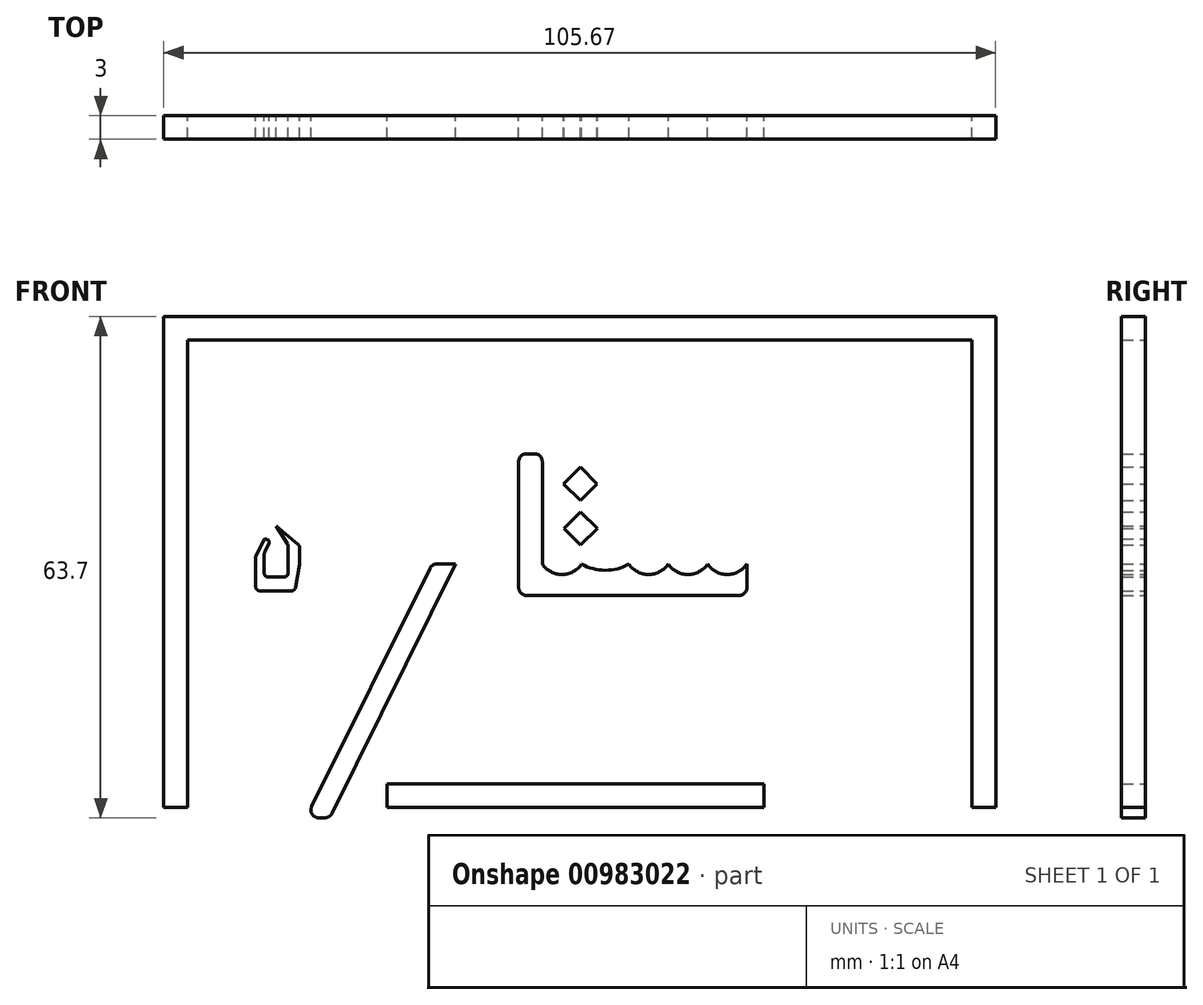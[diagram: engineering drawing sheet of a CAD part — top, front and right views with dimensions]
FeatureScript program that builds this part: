
annotation { "Feature Type Name" : "Feature", "Feature Type Description" : "" }
export const myFeature = defineFeature(function(context is Context, id is Id, definition is map)
    precondition{}
    {
        {
            var Q0;
            Q0=qCreatedBy(makeId("Front.planeOp"),FACE);
            var sketch = newSketch(context, id + "F0", { "sketchPlane" : qUnion([Q0])});
            skArc(sketch, "E0", {"start": v(-5, 0) * mm, "mid": v(-2.5, -1.34) * mm, "end": v(0, 0) * mm});
            skArc(sketch, "E1", {"start": v(-10, 0) * mm, "mid": v(-7.5, -1.34) * mm, "end": v(-5, 0) * mm});
            skArc(sketch, "E2", {"start": v(-15, 0) * mm, "mid": v(-12.5, -1.34) * mm, "end": v(-10, 0) * mm});
            skArc(sketch, "E3", {"start": v(-21, 0) * mm, "mid": v(-18, -0.8) * mm, "end": v(-15, 0) * mm});
            skArc(sketch, "E4", {"start": v(-26, 0) * mm, "mid": v(-23.5, -1.34) * mm, "end": v(-21, 0) * mm});
            skLineSegment(sketch, "E5", {"start": v(-26, 0) * mm, "end": v(-26, 13) * mm});
            skLineSegment(sketch, "E6", {"start": v(-29, 13) * mm, "end": v(-29, -3) * mm});
            skLineSegment(sketch, "E7", {"start": v(-28, -4) * mm, "end": v(-1, -4) * mm});
            skLineSegment(sketch, "E8", {"start": v(-27, 14) * mm, "end": v(-28, 14) * mm});
            skLineSegment(sketch, "E9", {"start": v(0, -3) * mm, "end": v(0, 0) * mm});
            skPoint(sketch, "E10.visualSharp", {"position": v(-29, 14) * mm});
            skArc(sketch, "E10.filletArc", {"start": v(-28, 14) * mm, "mid": v(-28.7, 13.7) * mm, "end": v(-29, 13) * mm});
            skPoint(sketch, "E11.visualSharp", {"position": v(-26, 14) * mm});
            skArc(sketch, "E11.filletArc", {"start": v(-26, 13) * mm, "mid": v(-26.3, 13.7) * mm, "end": v(-27, 14) * mm});
            skPoint(sketch, "E12.visualSharp", {"position": v(-29, -4) * mm});
            skArc(sketch, "E12.filletArc", {"start": v(-29, -3) * mm, "mid": v(-28.7, -3.7) * mm, "end": v(-28, -4) * mm});
            skPoint(sketch, "E13.visualSharp", {"position": v(0, -4) * mm});
            skArc(sketch, "E13.filletArc", {"start": v(-1, -4) * mm, "mid": v(-0.3, -3.7) * mm, "end": v(0, -3) * mm});
            skLineSegment(sketch, "E14", {"start": v(-39.38, 0) * mm, "end": v(-37, 0) * mm});
            skLineSegment(sketch, "E15", {"start": v(-37, 0) * mm, "end": v(-52.72, -31.7) * mm});
            skLineSegment(sketch, "E16", {"start": v(-53.62, -32.25) * mm, "end": v(-54.39, -32.25) * mm});
            skLineSegment(sketch, "E17", {"start": v(-55.28, -30.8) * mm, "end": v(-40.28, -0.56) * mm});
            skPoint(sketch, "E18.visualSharp", {"position": v(-40, 0) * mm});
            skArc(sketch, "E18.filletArc", {"start": v(-39.38, 0) * mm, "mid": v(-39.9, -0.15) * mm, "end": v(-40.28, -0.56) * mm});
            skPoint(sketch, "E19.visualSharp", {"position": v(-56, -32.25) * mm});
            skArc(sketch, "E19.filletArc", {"start": v(-55.28, -30.8) * mm, "mid": v(-55.24, -31.78) * mm, "end": v(-54.39, -32.25) * mm});
            skPoint(sketch, "E20.visualSharp", {"position": v(-53, -32.25) * mm});
            skArc(sketch, "E20.filletArc", {"start": v(-53.62, -32.25) * mm, "mid": v(-53.1, -32.1) * mm, "end": v(-52.72, -31.7) * mm});
            skLineSegment(sketch, "E21.bottom", {"start": v(-21.12, 6.63) * mm, "end": v(-19, 4.51) * mm});
            skLineSegment(sketch, "E21.top", {"start": v(-23.24, 4.51) * mm, "end": v(-21.12, 2.39) * mm});
            skLineSegment(sketch, "E21.left", {"start": v(-21.12, 6.63) * mm, "end": v(-23.24, 4.51) * mm});
            skLineSegment(sketch, "E21.right", {"start": v(-19, 4.51) * mm, "end": v(-21.12, 2.39) * mm});
            skLineSegment(sketch, "E22.bottom", {"start": v(-21.17, 12.3) * mm, "end": v(-19.05, 10.17) * mm});
            skLineSegment(sketch, "E22.top", {"start": v(-23.3, 10.17) * mm, "end": v(-21.17, 8.05) * mm});
            skLineSegment(sketch, "E22.left", {"start": v(-21.17, 12.3) * mm, "end": v(-23.3, 10.17) * mm});
            skLineSegment(sketch, "E22.right", {"start": v(-19.05, 10.17) * mm, "end": v(-21.17, 8.05) * mm});
            skLineSegment(sketch, "E23.bottom", {"start": v(-71.08, 31.45) * mm, "end": v(-74.08, 31.45) * mm});
            skLineSegment(sketch, "E23.top", {"start": v(-71.08, -30.93) * mm, "end": v(-74.08, -30.93) * mm});
            skLineSegment(sketch, "E23.left", {"start": v(-71.08, 31.45) * mm, "end": v(-71.08, -30.93) * mm});
            skLineSegment(sketch, "E23.right", {"start": v(-74.08, 31.45) * mm, "end": v(-74.08, -30.93) * mm});
            skLineSegment(sketch, "E24.bottom", {"start": v(-71.08, 31.45) * mm, "end": v(28.6, 31.45) * mm});
            skLineSegment(sketch, "E24.top", {"start": v(-71.08, 28.45) * mm, "end": v(28.6, 28.45) * mm});
            skLineSegment(sketch, "E24.left", {"start": v(-71.08, 31.45) * mm, "end": v(-71.08, 28.45) * mm});
            skLineSegment(sketch, "E24.right", {"start": v(28.6, 31.45) * mm, "end": v(28.6, 28.45) * mm});
            skLineSegment(sketch, "E25.bottom", {"start": v(28.6, 31.45) * mm, "end": v(31.6, 31.45) * mm});
            skLineSegment(sketch, "E25.top", {"start": v(28.6, -30.93) * mm, "end": v(31.6, -30.93) * mm});
            skLineSegment(sketch, "E25.left", {"start": v(28.6, 31.45) * mm, "end": v(28.6, -30.93) * mm});
            skLineSegment(sketch, "E25.right", {"start": v(31.6, 31.45) * mm, "end": v(31.6, -30.93) * mm});
            skLineSegment(sketch, "E26.bottom", {"start": v(-45.73, -27.93) * mm, "end": v(2.13, -27.93) * mm});
            skLineSegment(sketch, "E26.top", {"start": v(-45.73, -30.93) * mm, "end": v(2.13, -30.93) * mm});
            skLineSegment(sketch, "E26.left", {"start": v(-45.73, -27.93) * mm, "end": v(-45.73, -30.93) * mm});
            skLineSegment(sketch, "E26.right", {"start": v(2.13, -27.93) * mm, "end": v(2.13, -30.93) * mm});
            skLineSegment(sketch, "E27", {"start": v(-59.84, 4.8) * mm, "end": v(-58.37, 2.54) * mm});
            skLineSegment(sketch, "E28", {"start": v(-58.3, 2.27) * mm, "end": v(-58.3, -1.16) * mm});
            skLineSegment(sketch, "E29", {"start": v(-58.8, -1.66) * mm, "end": v(-60.82, -1.66) * mm});
            skLineSegment(sketch, "E30", {"start": v(-61.32, -1.16) * mm, "end": v(-61.32, 1.14) * mm});
            skLineSegment(sketch, "E31", {"start": v(-61.22, 1.57) * mm, "end": v(-60.7, 2.64) * mm});
            skLineSegment(sketch, "E32", {"start": v(-60.85, 3.04) * mm, "end": v(-61.03, 3.13) * mm});
            skLineSegment(sketch, "E33", {"start": v(-61.43, 2.99) * mm, "end": v(-62.37, 1.02) * mm});
            skLineSegment(sketch, "E34", {"start": v(-62.4, 0.9) * mm, "end": v(-62.4, -1.66) * mm});
            skLineSegment(sketch, "E35", {"start": v(-62.4, -1.66) * mm, "end": v(-62.4, -2.9) * mm});
            skLineSegment(sketch, "E36", {"start": v(-61.9, -3.4) * mm, "end": v(-57.84, -3.4) * mm});
            skLineSegment(sketch, "E37", {"start": v(-57.35, -3) * mm, "end": v(-56.82, -0.04) * mm});
            skLineSegment(sketch, "E38", {"start": v(-56.81, 0.04) * mm, "end": v(-56.81, 2.07) * mm});
            skLineSegment(sketch, "E39", {"start": v(-57, 2.45) * mm, "end": v(-59.84, 4.8) * mm});
            skPoint(sketch, "E40.visualSharp", {"position": v(-61.32, 1.37) * mm});
            skArc(sketch, "E40.filletArc", {"start": v(-61.22, 1.57) * mm, "mid": v(-61.3, 1.36) * mm, "end": v(-61.32, 1.14) * mm});
            skPoint(sketch, "E41.visualSharp", {"position": v(-60.58, 2.91) * mm});
            skArc(sketch, "E41.filletArc", {"start": v(-60.7, 2.64) * mm, "mid": v(-60.7, 2.87) * mm, "end": v(-60.85, 3.04) * mm});
            skPoint(sketch, "E42.visualSharp", {"position": v(-61.3, 3.26) * mm});
            skArc(sketch, "E42.filletArc", {"start": v(-61.03, 3.13) * mm, "mid": v(-61.26, 3.14) * mm, "end": v(-61.43, 2.99) * mm});
            skPoint(sketch, "E43.visualSharp", {"position": v(-62.4, 0.96) * mm});
            skArc(sketch, "E43.filletArc", {"start": v(-62.37, 1.02) * mm, "mid": v(-62.39, 0.96) * mm, "end": v(-62.4, 0.9) * mm});
            skPoint(sketch, "E44.visualSharp", {"position": v(-61.32, -1.66) * mm});
            skArc(sketch, "E44.filletArc", {"start": v(-61.32, -1.16) * mm, "mid": v(-61.17, -1.51) * mm, "end": v(-60.82, -1.66) * mm});
            skPoint(sketch, "E45.visualSharp", {"position": v(-58.3, -1.66) * mm});
            skArc(sketch, "E45.filletArc", {"start": v(-58.8, -1.66) * mm, "mid": v(-58.44, -1.51) * mm, "end": v(-58.3, -1.16) * mm});
            skPoint(sketch, "E46.visualSharp", {"position": v(-58.3, 2.42) * mm});
            skArc(sketch, "E46.filletArc", {"start": v(-58.3, 2.27) * mm, "mid": v(-58.31, 2.41) * mm, "end": v(-58.37, 2.54) * mm});
            skPoint(sketch, "E47.visualSharp", {"position": v(-56.81, 2.3) * mm});
            skArc(sketch, "E47.filletArc", {"start": v(-56.81, 2.07) * mm, "mid": v(-56.86, 2.28) * mm, "end": v(-57, 2.45) * mm});
            skPoint(sketch, "E48.visualSharp", {"position": v(-56.81, 0) * mm});
            skArc(sketch, "E48.filletArc", {"start": v(-56.82, -0.04) * mm, "mid": v(-56.81, 0) * mm, "end": v(-56.81, 0.04) * mm});
            skPoint(sketch, "E49.visualSharp", {"position": v(-57.42, -3.4) * mm});
            skArc(sketch, "E49.filletArc", {"start": v(-57.84, -3.4) * mm, "mid": v(-57.52, -3.3) * mm, "end": v(-57.35, -3) * mm});
            skPoint(sketch, "E50.visualSharp", {"position": v(-62.4, -3.4) * mm});
            skArc(sketch, "E50.filletArc", {"start": v(-62.4, -2.9) * mm, "mid": v(-62.25, -3.26) * mm, "end": v(-61.9, -3.4) * mm});
            skSolve(sketch);
        }
        {
            var Q0;
            Q0 = qSketchRegion(id + "F0", true);
            extrude(context, id + "F1", {"entities" : qUnion([Q0]), "depth" : 3 * mm, "offsetDistance" : 25 * mm});
        }
    });
